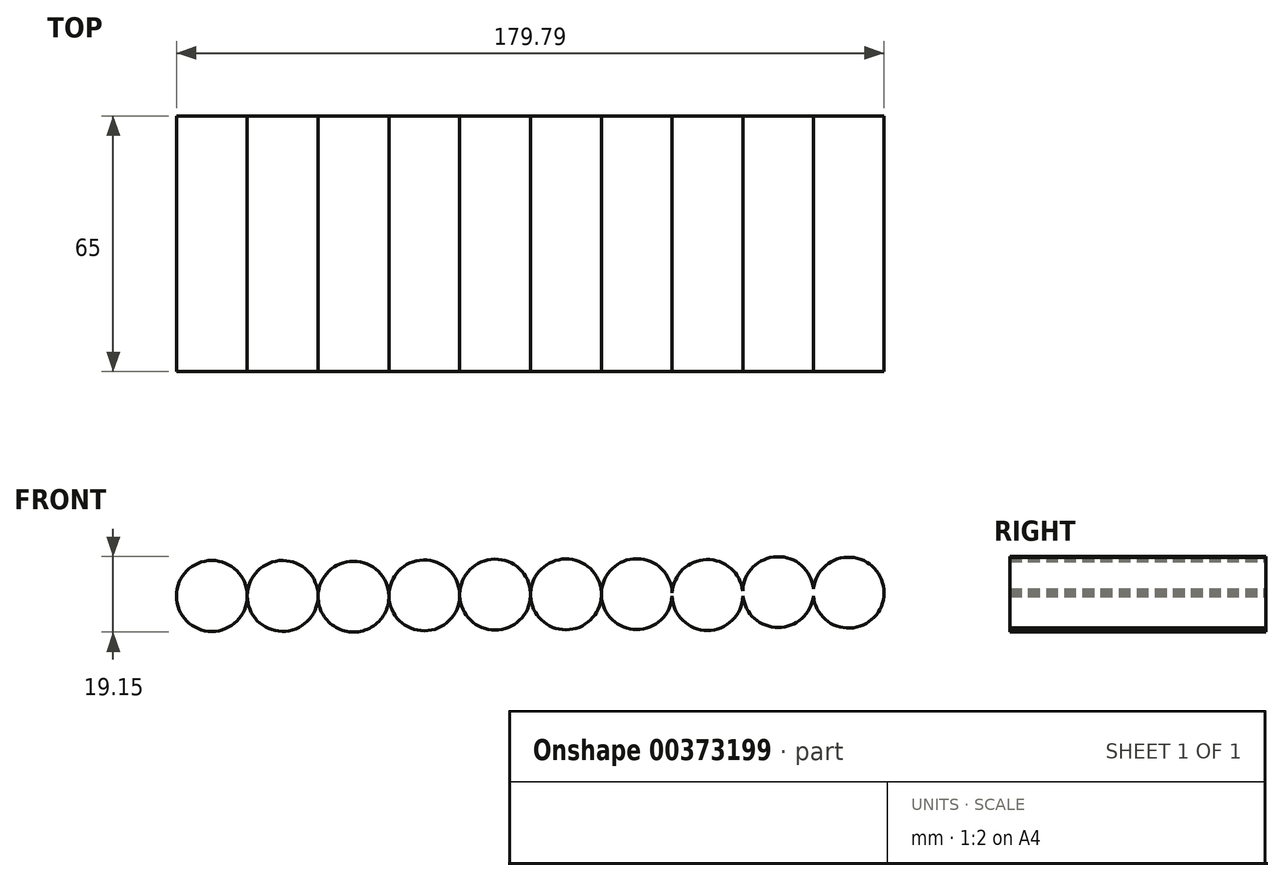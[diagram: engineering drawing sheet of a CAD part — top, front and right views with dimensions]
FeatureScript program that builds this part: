
annotation { "Feature Type Name" : "Feature", "Feature Type Description" : "" }
export const myFeature = defineFeature(function(context is Context, id is Id, definition is map)
    precondition{}
    {
        {
            var Q0;
            Q0=qCreatedBy(makeId("Front.planeOp"),FACE);
            var sketch = newSketch(context, id + "F0", { "sketchPlane" : qUnion([Q0])});
            skCircle(sketch, "E0", {"center": v(0, 0) * mm, "radius": 9 * mm});
            skCircle(sketch, "E1", {"center": v(18, 0) * mm, "radius": 9 * mm});
            skPoint(sketch, "E1.first.point", {"position": v(9, 0) * mm});
            skPoint(sketch, "E1.second.point", {"position": v(27, 0) * mm});
            skPoint(sketch, "E1.third.point", {"position": v(10.52, 5) * mm});
            skCircle(sketch, "E2", {"center": v(36, -0.17) * mm, "radius": 9 * mm});
            skPoint(sketch, "E2.second.point", {"position": v(45, 0) * mm});
            skPoint(sketch, "E2.third.point", {"position": v(37.5, 8.7) * mm});
            skCircle(sketch, "E3", {"center": v(54, 0.14) * mm, "radius": 9 * mm});
            skPoint(sketch, "E3.second.point", {"position": v(63, 0) * mm});
            skPoint(sketch, "E3.third.point", {"position": v(57.03, 8.61) * mm});
            skCircle(sketch, "E4", {"center": v(72, 0.36) * mm, "radius": 9 * mm});
            skPoint(sketch, "E4.second.point", {"position": v(80.98, 0) * mm});
            skPoint(sketch, "E4.third.point", {"position": v(69.58, 9.03) * mm});
            skCircle(sketch, "E5", {"center": v(89.98, 0.39) * mm, "radius": 9 * mm});
            skPoint(sketch, "E5.second.point", {"position": v(98.97, 0) * mm});
            skPoint(sketch, "E5.third.point", {"position": v(95.32, 7.63) * mm});
            skCircle(sketch, "E6", {"center": v(107.96, 0.46) * mm, "radius": 9 * mm});
            skPoint(sketch, "E6.second.point", {"position": v(116.94, 0) * mm});
            skPoint(sketch, "E6.third.point", {"position": v(106.95, -8.48) * mm});
            skCircle(sketch, "E7", {"center": v(125.94, 0.25) * mm, "radius": 9 * mm});
            skPoint(sketch, "E7.second.point", {"position": v(134.94, 0) * mm});
            skPoint(sketch, "E7.third.point", {"position": v(124.62, 9.16) * mm});
            skCircle(sketch, "E8", {"center": v(143.88, 0.98) * mm, "radius": 9 * mm});
            skPoint(sketch, "E8.second.point", {"position": v(152.65, -1.06) * mm});
            skPoint(sketch, "E8.third.point", {"position": v(151.58, 5.65) * mm});
            skCircle(sketch, "E9", {"center": v(161.8, 0.84) * mm, "radius": 9 * mm});
            skPoint(sketch, "E9.first.point", {"position": v(152.83, 0) * mm});
            skPoint(sketch, "E9.second.point", {"position": v(170.65, 2.4) * mm});
            skPoint(sketch, "E9.third.point", {"position": v(168.8, -4.8) * mm});
            skSolve(sketch);
        }
        {
            var Q0;
            Q0=makeQuery(id+"F0.imprint","IMPRINT",FACE,{"disambiguationData":[TD([[makeQuery(id+"F0.imprint","IMPRINT",EDGE,{"derivedFrom":sQuery(id+"F0.wireOp",EDGE,"E0")}),1.0]])]});
            var Q1;
            {var subQ0=sQuery(id+"F0.wireOp",EDGE,"E1");var subQ1=makeQuery(id+"F0.imprint","INTERSECT",VERTEX,{"derivedFrom":[sQuery(id+"F0.wireOp",EDGE,"E0"),subQ0]});Q1=makeQuery(id+"F0.imprint","IMPRINT",FACE,{"disambiguationData":[TD([[makeQuery(id+"F0.imprint","IMPRINT",EDGE,{"disambiguationData":[TD([[subQ1,1.0]])],"derivedFrom":subQ0}),1.0]])]});}
            var Q2;
            {var subQ0=sQuery(id+"F0.wireOp",EDGE,"E2");var subQ1=sQuery(id+"F0.wireOp",EDGE,"E1");var subQ2=makeQuery(id+"F0.imprint","INTERSECT",VERTEX,{"disambiguationData":[OD(0.0)],"derivedFrom":[subQ1,subQ0]});Q2=makeQuery(id+"F0.imprint","IMPRINT",FACE,{"disambiguationData":[TD([[makeQuery(id+"F0.imprint","IMPRINT",EDGE,{"disambiguationData":[TD([[subQ2,1.0]])],"derivedFrom":subQ1}),-1.0]])]});}
            var Q3;
            {var subQ0=sQuery(id+"F0.wireOp",EDGE,"E3");var subQ1=sQuery(id+"F0.wireOp",EDGE,"E2");var subQ2=makeQuery(id+"F0.imprint","INTERSECT",VERTEX,{"disambiguationData":[OD(0.0)],"derivedFrom":[subQ1,subQ0]});Q3=makeQuery(id+"F0.imprint","IMPRINT",FACE,{"disambiguationData":[TD([[makeQuery(id+"F0.imprint","IMPRINT",EDGE,{"disambiguationData":[TD([[subQ2,1.0]])],"derivedFrom":subQ0}),1.0]])]});}
            var Q4;
            {var subQ0=sQuery(id+"F0.wireOp",EDGE,"E4");var subQ1=sQuery(id+"F0.wireOp",EDGE,"E3");var subQ2=makeQuery(id+"F0.imprint","INTERSECT",VERTEX,{"disambiguationData":[OD(0.0)],"derivedFrom":[subQ1,subQ0]});Q4=makeQuery(id+"F0.imprint","IMPRINT",FACE,{"disambiguationData":[TD([[makeQuery(id+"F0.imprint","IMPRINT",EDGE,{"disambiguationData":[TD([[subQ2,1.0]])],"derivedFrom":subQ1}),-1.0]])]});}
            var Q5;
            {var subQ0=sQuery(id+"F0.wireOp",EDGE,"E5");var subQ1=sQuery(id+"F0.wireOp",EDGE,"E4");var subQ2=makeQuery(id+"F0.imprint","INTERSECT",VERTEX,{"disambiguationData":[OD(0.0)],"derivedFrom":[subQ1,subQ0]});Q5=makeQuery(id+"F0.imprint","IMPRINT",FACE,{"disambiguationData":[TD([[makeQuery(id+"F0.imprint","IMPRINT",EDGE,{"disambiguationData":[TD([[subQ2,1.0]])],"derivedFrom":subQ1}),-1.0]])]});}
            extrude(context, id + "F1", {"entities" : qUnion([Q0, Q1, Q2, Q3, Q4, Q5]), "depth" : 65 * mm});
        }
        {
            var Q0;
            Q0 = qSketchRegion(id + "F0", true);
            extrude(context, id + "F2", {"entities" : qUnion([Q0]), "depth" : 65 * mm});
        }
    });
